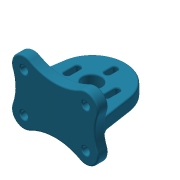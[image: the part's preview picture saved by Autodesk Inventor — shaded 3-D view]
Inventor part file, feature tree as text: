
AUTODESK INVENTOR PART (.ipt)
format: ipt  version: 2014 (Build 180170000, 170)  size: 581,632 bytes
history: native  units: mm
features: fillet x8, extrude x6, sketch x6, chamfer x1
ambient origin geometry x8: Origin, YZ Plane, XZ Plane, XY Plane, X Axis, Y Axis, Z Axis, Center Point
bodies: Solid1 (feature_tree)
feature tree (21):
  extrude  "Extrusion1"  Depth=41.0mm
  extrude  "Extrusion2"  Depth=6.0mm
  extrude  "Extrusion3"  Depth=35.0mm
  extrude  "Extrusion4"  Depth=22.0mm
  extrude  "Extrusion5"  Depth=50.0mm
  extrude  "Extrusion6"  Depth=0.5mm
  chamfer  "Chamfer1"  Distance=7.5mm
  fillet  "Fillet1"  Radius=3.6mm
  fillet  "Fillet2"  Radius=4.75mm
  fillet  "Fillet3"  Radius=2.5mm
  fillet  "Fillet4"  Radius=2.5mm
  fillet  "Fillet5"  Radius=13.0mm
  fillet  "Fillet6"  Radius=13.0mm
  fillet  "Fillet7"  Radius=7.0mm
  fillet  "Fillet8"  Radius=7.5mm
  sketch  "Sketch1"  dims[d0=26.0mm d1=41.0mm]
  sketch  "Sketch2"  dims[d2=4.5mm d3=6.0mm]
  sketch  "Sketch3"  dims[d4=30.0mm d5=35.0mm]
  sketch  "Sketch4"  dims[d6=7.0mm d7=0.0mm d8=22.0mm]
  sketch  "Sketch7"  dims[d9=18.0mm d10=50.0mm]
  sketch  "Sketch9"  dims[d11=8.5mm d12=0.0mm d13=12.0mm d14=7.5mm d15=0.0mm d16=3.6mm d17=4.75mm d18=2.5mm d19=2.5mm d20=13.0mm d21=13.0mm d22=7.0mm d23=7.5mm d24=0.0mm d25=5.75mm d26=3.5mm d27=0.0mm d28=10.5mm d29=2.0mm d30=0.0mm d31=3.0mm d32=2.0mm d33=45.0deg d34=1.0mm d35=0.75mm d36=1.0mm d37=1.0mm d38=1.0mm d39=1.0mm d40=0.5mm d41=0.5mm]
